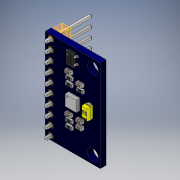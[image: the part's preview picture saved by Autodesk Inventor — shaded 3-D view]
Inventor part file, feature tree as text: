
AUTODESK INVENTOR PART (.ipt)
format: ipt  version: 2018 (Build 220112000, 112)  size: 1,402,368 bytes
history: native  units: mm
features: other x36, hole x20
ambient origin geometry x8: Origin, YZ Plane, XZ Plane, XY Plane, X Axis, Y Axis, Z Axis, Center Point
bodies: Solid1 (feature_tree), Solid2 (feature_tree), Solid3 (feature_tree), Solid4 (feature_tree), Solid5 (feature_tree), Solid6 (feature_tree), Solid7 (feature_tree), Solid8 (feature_tree), Solid9 (feature_tree), Solid10 (feature_tree), Solid11 (feature_tree), Solid12 (feature_tree), Solid13 (feature_tree), Solid14 (feature_tree), Solid15 (feature_tree), Solid16 (feature_tree), Solid17 (feature_tree), Solid18 (feature_tree), Solid19 (feature_tree), Solid20 (feature_tree), Solid21 (feature_tree), Solid22 (feature_tree), Solid23 (feature_tree), Solid24 (feature_tree), Solid25 (feature_tree), Solid26 (feature_tree), Solid27 (feature_tree), Solid28 (feature_tree), Solid29 (feature_tree), Solid30 (feature_tree), Solid31 (feature_tree), Solid32 (feature_tree), Solid33 (feature_tree), Solid34 (feature_tree), Solid35 (feature_tree)
feature tree (56):
  other  "MPU-9250.iam"
  other  "board.ipt:1"
  hole  "hole_plating:1"  [1 undecoded]
  hole  "hole_plating:2"  [1 undecoded]
  hole  "hole_plating:3"  [1 undecoded]
  hole  "hole_plating:4"  [1 undecoded]
  hole  "hole_plating:5"  [1 undecoded]
  hole  "hole_plating:6"  [1 undecoded]
  hole  "hole_plating:7"  [1 undecoded]
  hole  "hole_plating:8"  [1 undecoded]
  hole  "hole_plating:9"  [1 undecoded]
  hole  "hole_plating:10"  [1 undecoded]
  hole  "hole_plating:11"  [1 undecoded]
  hole  "hole_plating:12"  [1 undecoded]
  hole  "hole_plating:13"  [1 undecoded]
  hole  "hole_plating:14"  [1 undecoded]
  hole  "hole_plating:15"  [1 undecoded]
  hole  "hole_plating:16"  [1 undecoded]
  hole  "hole_plating:17"  [1 undecoded]
  hole  "hole_plating:18"  [1 undecoded]
  hole  "hole_plating:19"  [1 undecoded]
  hole  "hole_plating:20"  [1 undecoded]
  other  "Pin Header 1x10 TH Pitch 2.54mm.ipt:1"
  other  "MPU-9250:1"
  other  "tantalum 10uF.ipt:1"
  other  "SOT23_5.ipt:1"
  other  "RESC-0603.ipt:1"
  other  "RESC-0603.ipt:2"
  other  "RESC-0603.ipt:3"
  other  "RESC-0603.ipt:4"
  other  "RESC-0603.ipt:5"
  other  "CAPC-0603-T0.9-BN.ipt:1"
  other  "CAPC-0603-T0.9-BN.ipt:2"
  other  "CAPC-0603-T0.9-BN.ipt:3"
  other  "CAPC-0603-T0.9-BN.ipt:4"
  other  "CAPC-0603-T0.9-BN.ipt:5"
  other  "Srf1"
  other  "Srf2"
  other  "Srf3"
  other  "Srf4"
  other  "Srf5"
  other  "Srf6"
  other  "Srf7"
  other  "Srf8"
  other  "Srf9"
  other  "Srf10"
  other  "Srf1::Derived"
  other  "Srf2::Derived"
  other  "Srf3::Derived"
  other  "Srf4::Derived"
  other  "Srf5::Derived"
  other  "Srf6::Derived"
  other  "Srf7::Derived"
  other  "Srf8::Derived"
  other  "Srf9::Derived"
  other  "Srf10::Derived"
note: 20 required parameter values undecoded (feature->parameter linkage not recoverable at this tier; creation-order binding heuristic only, values carry confidence <= 0.55)
